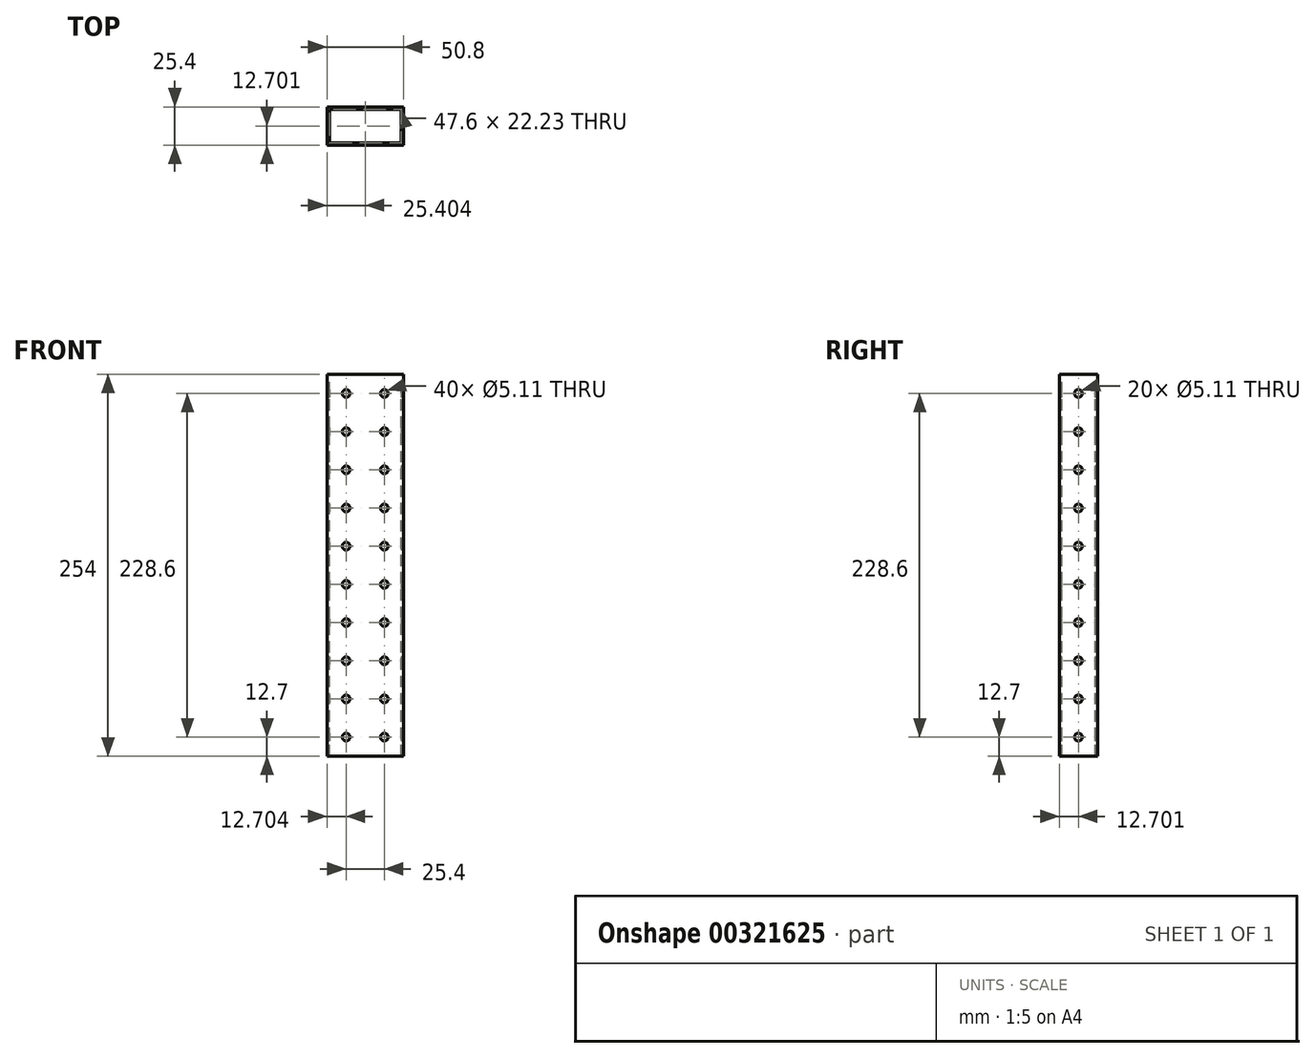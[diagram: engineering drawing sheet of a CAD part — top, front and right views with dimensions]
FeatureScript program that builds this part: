
annotation { "Feature Type Name" : "Feature", "Feature Type Description" : "" }
export const myFeature = defineFeature(function(context is Context, id is Id, definition is map)
    precondition{}
    {
        {
            var Q0;
            Q0=qCreatedBy(makeId("Top.planeOp"),FACE);
            var sketch = newSketch(context, id + "F0", { "sketchPlane" : qUnion([Q0])});
            skLineSegment(sketch, "E0.bottom", {"start": v(-18.08, 33.34) * mm, "end": v(-68.88, 33.34) * mm});
            skLineSegment(sketch, "E0.top", {"start": v(-18.08, 58.74) * mm, "end": v(-68.88, 58.74) * mm});
            skLineSegment(sketch, "E0.left", {"start": v(-18.08, 33.34) * mm, "end": v(-18.08, 58.74) * mm});
            skLineSegment(sketch, "E0.right", {"start": v(-68.88, 33.34) * mm, "end": v(-68.88, 58.74) * mm});
            skPoint(sketch, "E0.middle", {"position": v(-43.48, 46.04) * mm});
            skSolve(sketch);
        }
        {
            var Q0;
            Q0=makeQuery(id+"F0.imprint","IMPRINT",FACE,{"disambiguationData":[TD([[makeQuery(id+"F0.imprint","IMPRINT",EDGE,{"derivedFrom":sQuery(id+"F0.wireOp",EDGE,"E0.bottom")}),-1.0]])]});
            extrude(context, id + "F1", {"entities" : qUnion([Q0]), "depth" : 254 * mm});
        }
        {
            var Q0;
            Q0=makeQuery(id+"F1.opExtrude","SWEPT_FACE",FACE,{"disambiguationData":[OSD([sQuery(id+"F0.wireOp",EDGE,"E0.bottom")])]});
            var sketch = newSketch(context, id + "F2", { "sketchPlane" : qUnion([Q0])});
            skCircle(sketch, "E1", {"center": v(-56.18, 241.3) * mm, "radius": 2.55 * mm});
            skCircle(sketch, "E2.0.1.0", {"center": v(-56.18, 215.9) * mm, "radius": 2.55 * mm});
            skCircle(sketch, "E2.0.2.0", {"center": v(-56.18, 190.5) * mm, "radius": 2.55 * mm});
            skCircle(sketch, "E2.0.3.0", {"center": v(-56.18, 165.1) * mm, "radius": 2.55 * mm});
            skCircle(sketch, "E2.0.4.0", {"center": v(-56.18, 139.7) * mm, "radius": 2.55 * mm});
            skCircle(sketch, "E2.0.5.0", {"center": v(-56.18, 114.3) * mm, "radius": 2.55 * mm});
            skCircle(sketch, "E2.0.6.0", {"center": v(-56.18, 88.9) * mm, "radius": 2.55 * mm});
            skCircle(sketch, "E2.0.7.0", {"center": v(-56.18, 63.5) * mm, "radius": 2.55 * mm});
            skCircle(sketch, "E2.0.8.0", {"center": v(-56.18, 38.1) * mm, "radius": 2.55 * mm});
            skCircle(sketch, "E2.0.9.0", {"center": v(-56.18, 12.7) * mm, "radius": 2.55 * mm});
            skCircle(sketch, "E2.1.0.0", {"center": v(-30.78, 241.3) * mm, "radius": 2.55 * mm});
            skCircle(sketch, "E2.1.1.0", {"center": v(-30.78, 215.9) * mm, "radius": 2.55 * mm});
            skCircle(sketch, "E2.1.2.0", {"center": v(-30.78, 190.5) * mm, "radius": 2.55 * mm});
            skCircle(sketch, "E2.1.3.0", {"center": v(-30.78, 165.1) * mm, "radius": 2.55 * mm});
            skCircle(sketch, "E2.1.4.0", {"center": v(-30.78, 139.7) * mm, "radius": 2.55 * mm});
            skCircle(sketch, "E2.1.5.0", {"center": v(-30.78, 114.3) * mm, "radius": 2.55 * mm});
            skCircle(sketch, "E2.1.6.0", {"center": v(-30.78, 88.9) * mm, "radius": 2.55 * mm});
            skCircle(sketch, "E2.1.7.0", {"center": v(-30.78, 63.5) * mm, "radius": 2.55 * mm});
            skCircle(sketch, "E2.1.8.0", {"center": v(-30.78, 38.1) * mm, "radius": 2.55 * mm});
            skCircle(sketch, "E2.1.9.0", {"center": v(-30.78, 12.7) * mm, "radius": 2.55 * mm});
            skLineSegment(sketch, "E2.direction1", {"start": v(-56.18, 241.3) * mm, "end": v(-30.78, 241.3) * mm, "construction": true});
            skLineSegment(sketch, "E2.direction2", {"start": v(-56.18, 241.3) * mm, "end": v(-56.18, 215.9) * mm, "construction": true});
            skSolve(sketch);
        }
        {
            var Q0;
            Q0=sQuery(id+"F2.wireOp",VERTEX,"E2.0.3.0.center");
            var Q1;
            Q1=sQuery(id+"F2.wireOp",VERTEX,"E2.0.6.0.center");
            var Q2;
            Q2=sQuery(id+"F2.wireOp",VERTEX,"E2.0.4.0.center");
            var Q3;
            Q3=sQuery(id+"F2.wireOp",VERTEX,"E2.0.5.0.center");
            var Q4;
            Q4=sQuery(id+"F2.wireOp",VERTEX,"E2.1.3.0.center");
            var Q5;
            Q5=sQuery(id+"F2.wireOp",VERTEX,"E2.1.5.0.center");
            var Q6;
            Q6=sQuery(id+"F2.wireOp",VERTEX,"E2.1.9.0.center");
            var Q7;
            Q7=sQuery(id+"F2.wireOp",VERTEX,"E2.1.7.0.center");
            var Q8;
            Q8=sQuery(id+"F2.wireOp",VERTEX,"E2.0.8.0.center");
            var Q9;
            Q9=sQuery(id+"F2.wireOp",VERTEX,"E2.0.7.0.center");
            var Q10;
            Q10=sQuery(id+"F2.wireOp",VERTEX,"E2.1.8.0.center");
            var Q11;
            Q11=sQuery(id+"F2.wireOp",VERTEX,"E2.1.6.0.center");
            var Q12;
            Q12=sQuery(id+"F2.wireOp",VERTEX,"E2.0.9.0.center");
            var Q13;
            Q13=sQuery(id+"F2.wireOp",VERTEX,"E2.1.4.0.center");
            var Q14;
            Q14=sQuery(id+"F2.wireOp",VERTEX,"E2.1.1.0.center");
            var Q15;
            Q15=sQuery(id+"F2.wireOp",VERTEX,"E2.1.2.0.center");
            var Q16;
            Q16=sQuery(id+"F2.wireOp",VERTEX,"E2.direction1.end");
            var Q17;
            Q17=sQuery(id+"F2.wireOp",VERTEX,"E1.center");
            var Q18;
            Q18=sQuery(id+"F2.wireOp",VERTEX,"E2.0.1.0.center");
            var Q19;
            Q19=sQuery(id+"F2.wireOp",VERTEX,"E2.0.2.0.center");
            var Q20;
            Q20=makeQuery(id+"F1.opExtrude","SWEPT_BODY",BODY,{"disambiguationData":[OSD([sQuery(id+"F0.wireOp",EDGE,"E0.bottom"),sQuery(id+"F0.wireOp",EDGE,"E0.top"),sQuery(id+"F0.wireOp",EDGE,"E0.left"),sQuery(id+"F0.wireOp",EDGE,"E0.right")])]});
            hole(context, id + "F3", {"style" : HoleStyle.SIMPLE, "endStyle" : HoleEndStyle.THROUGH, "holeDiameter" : 5.1 * mm, "tappedDepth" : 12.7 * mm, "tapClearance" : 3, "locations" : qUnion([Q0, Q1, Q2, Q3, Q4, Q5, Q6, Q7, Q8, Q9, Q10, Q11, Q12, Q13, Q14, Q15, Q16, Q17, Q18, Q19]), "scope" : qUnion([Q20])});
        }
        {
            var Q0;
            Q0=makeQuery(id+"F1.opExtrude","CAP_FACE",FACE,{"disambiguationData":[OSD([sQuery(id+"F0.wireOp",EDGE,"E0.bottom"),sQuery(id+"F0.wireOp",EDGE,"E0.top"),sQuery(id+"F0.wireOp",EDGE,"E0.left"),sQuery(id+"F0.wireOp",EDGE,"E0.right")])],"isStart":false});
            var sketch = newSketch(context, id + "F4", { "sketchPlane" : qUnion([Q0])});
            skPoint(sketch, "E3.cornerSnap0", {"position": v(-18.08, 46.04) * mm});
            skLineSegment(sketch, "E4.bottom", {"start": v(-67.28, 57.15) * mm, "end": v(-19.68, 57.15) * mm});
            skLineSegment(sketch, "E4.top", {"start": v(-67.28, 34.93) * mm, "end": v(-19.68, 34.93) * mm});
            skLineSegment(sketch, "E4.left", {"start": v(-67.28, 57.15) * mm, "end": v(-67.28, 34.93) * mm});
            skLineSegment(sketch, "E4.right", {"start": v(-19.68, 57.15) * mm, "end": v(-19.68, 34.93) * mm});
            skSolve(sketch);
        }
        {
            var Q0;
            Q0=makeQuery(id+"F4.imprint","IMPRINT",FACE,{"disambiguationData":[TD([[makeQuery(id+"F4.imprint","IMPRINT",EDGE,{"derivedFrom":sQuery(id+"F4.wireOp",EDGE,"E4.bottom")}),-1.0]])]});
            extrude(context, id + "F5", {"entities" : qUnion([Q0]), "operationType" : NewBodyOperationType.REMOVE, "oppositeDirection" : true, "depth" : 254 * mm});
        }
        {
            var Q0;
            Q0=makeQuery(id+"F1.opExtrude","SWEPT_FACE",FACE,{"disambiguationData":[OSD([sQuery(id+"F0.wireOp",EDGE,"E0.right")])]});
            var sketch = newSketch(context, id + "F6", { "sketchPlane" : qUnion([Q0])});
            skCircle(sketch, "E5", {"center": v(-46.04, 241.3) * mm, "radius": 2.55 * mm});
            skCircle(sketch, "E6.0.1.0", {"center": v(-46.04, 215.9) * mm, "radius": 2.55 * mm});
            skCircle(sketch, "E6.0.2.0", {"center": v(-46.04, 190.5) * mm, "radius": 2.55 * mm});
            skCircle(sketch, "E6.0.3.0", {"center": v(-46.04, 165.1) * mm, "radius": 2.55 * mm});
            skCircle(sketch, "E6.0.4.0", {"center": v(-46.04, 139.7) * mm, "radius": 2.55 * mm});
            skCircle(sketch, "E6.0.5.0", {"center": v(-46.04, 114.3) * mm, "radius": 2.55 * mm});
            skCircle(sketch, "E6.0.6.0", {"center": v(-46.04, 88.9) * mm, "radius": 2.55 * mm});
            skCircle(sketch, "E6.0.7.0", {"center": v(-46.04, 63.5) * mm, "radius": 2.55 * mm});
            skCircle(sketch, "E6.0.8.0", {"center": v(-46.04, 38.1) * mm, "radius": 2.55 * mm});
            skCircle(sketch, "E6.0.9.0", {"center": v(-46.04, 12.7) * mm, "radius": 2.55 * mm});
            skLineSegment(sketch, "E6.direction1", {"start": v(-46.04, 241.3) * mm, "end": v(-20.64, 241.3) * mm, "construction": true});
            skLineSegment(sketch, "E6.direction2", {"start": v(-46.04, 241.3) * mm, "end": v(-46.04, 215.9) * mm, "construction": true});
            skSolve(sketch);
        }
        {
            var Q0;
            Q0=sQuery(id+"F6.wireOp",VERTEX,"E6.direction1.start");
            var Q1;
            Q1=sQuery(id+"F6.wireOp",VERTEX,"E6.0.4.0.center");
            var Q2;
            Q2=sQuery(id+"F6.wireOp",VERTEX,"E6.0.3.0.center");
            var Q3;
            Q3=sQuery(id+"F6.wireOp",VERTEX,"E6.0.6.0.center");
            var Q4;
            Q4=sQuery(id+"F6.wireOp",VERTEX,"E6.0.5.0.center");
            var Q5;
            Q5=sQuery(id+"F6.wireOp",VERTEX,"E6.0.7.0.center");
            var Q6;
            Q6=sQuery(id+"F6.wireOp",VERTEX,"E6.0.2.0.center");
            var Q7;
            Q7=sQuery(id+"F6.wireOp",VERTEX,"E6.0.1.0.center");
            var Q8;
            Q8=sQuery(id+"F6.wireOp",VERTEX,"E6.0.8.0.center");
            var Q9;
            Q9=sQuery(id+"F6.wireOp",VERTEX,"E6.direction1.end");
            var Q10;
            Q10=sQuery(id+"F6.wireOp",VERTEX,"E6.0.9.0.center");
            var Q11;
            Q11=makeQuery(id+"F1.opExtrude","SWEPT_BODY",BODY,{"disambiguationData":[OSD([sQuery(id+"F0.wireOp",EDGE,"E0.bottom"),sQuery(id+"F0.wireOp",EDGE,"E0.top"),sQuery(id+"F0.wireOp",EDGE,"E0.left"),sQuery(id+"F0.wireOp",EDGE,"E0.right")])]});
            hole(context, id + "F7", {"style" : HoleStyle.SIMPLE, "endStyle" : HoleEndStyle.THROUGH, "holeDiameter" : 5.1 * mm, "tappedDepth" : 12.7 * mm, "tapClearance" : 3, "locations" : qUnion([Q0, Q1, Q2, Q3, Q4, Q5, Q6, Q7, Q8, Q9, Q10]), "scope" : qUnion([Q11])});
        }
    });
